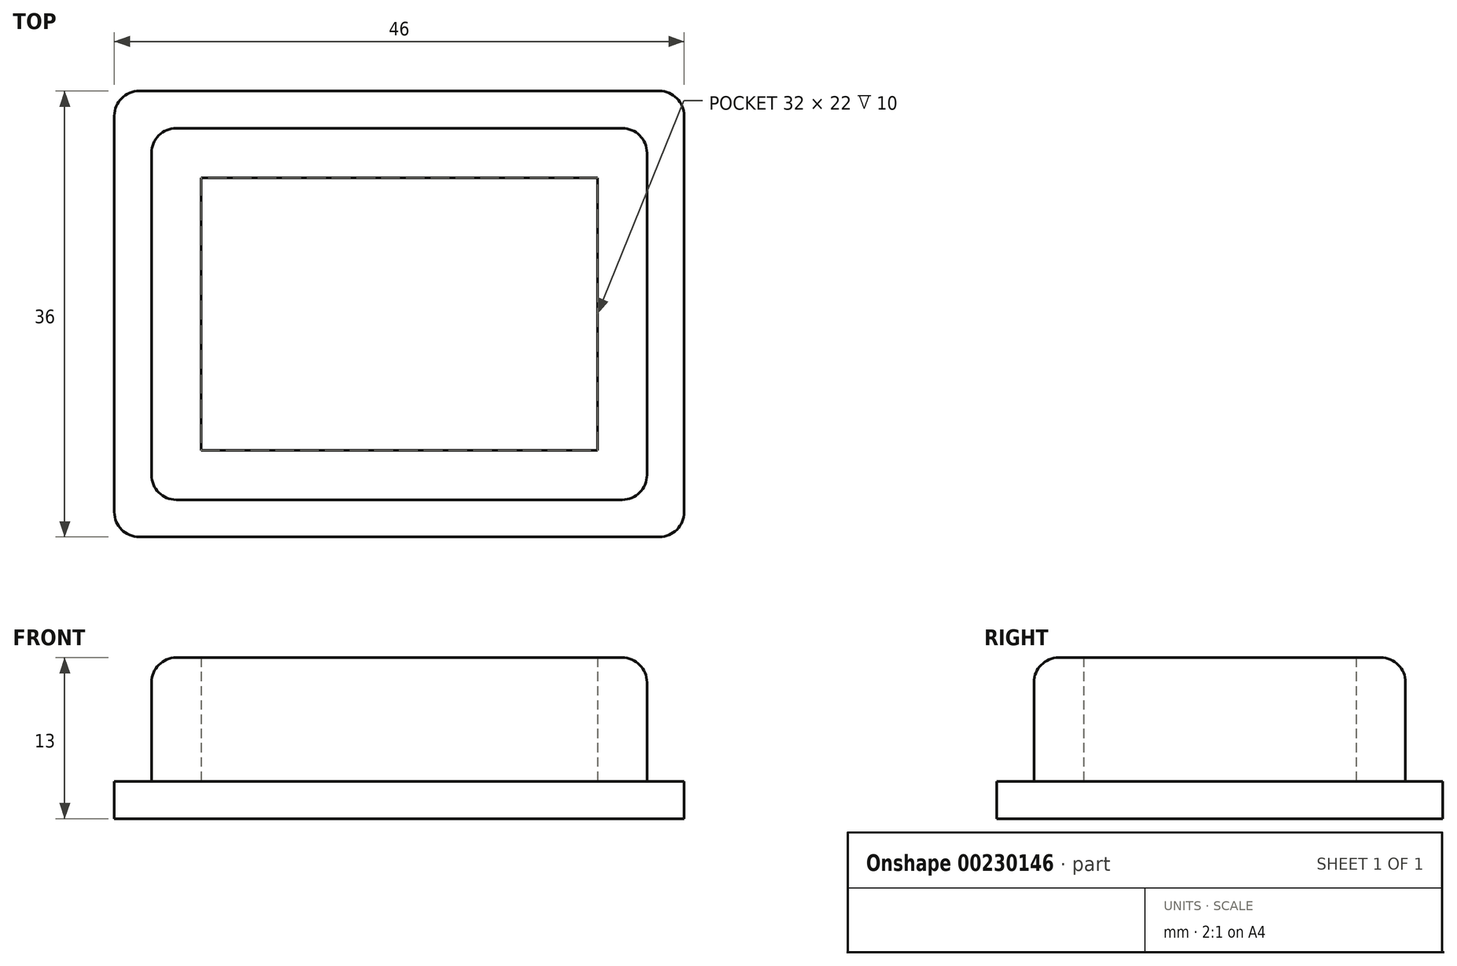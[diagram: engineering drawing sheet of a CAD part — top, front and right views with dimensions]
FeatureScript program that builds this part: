
annotation { "Feature Type Name" : "Feature", "Feature Type Description" : "" }
export const myFeature = defineFeature(function(context is Context, id is Id, definition is map)
    precondition{}
    {
        {
            var Q0;
            Q0=qCreatedBy(makeId("Top.planeOp"),FACE);
            var sketch = newSketch(context, id + "F0", { "sketchPlane" : qUnion([Q0])});
            skLineSegment(sketch, "E0.bottom", {"start": v(20, -15) * mm, "end": v(-20, -15) * mm});
            skLineSegment(sketch, "E0.top", {"start": v(20, 15) * mm, "end": v(-20, 15) * mm});
            skLineSegment(sketch, "E0.left", {"start": v(20, -15) * mm, "end": v(20, 15) * mm});
            skLineSegment(sketch, "E0.right", {"start": v(-20, -15) * mm, "end": v(-20, 15) * mm});
            skPoint(sketch, "E0.middle", {"position": v(0, 0) * mm});
            skLineSegment(sketch, "E1.0", {"start": v(-16, -11) * mm, "end": v(-16, 11) * mm});
            skLineSegment(sketch, "E1.1", {"start": v(16, -11) * mm, "end": v(-16, -11) * mm});
            skLineSegment(sketch, "E1.2", {"start": v(16, -11) * mm, "end": v(16, 11) * mm});
            skLineSegment(sketch, "E1.3", {"start": v(16, 11) * mm, "end": v(-16, 11) * mm});
            skLineSegment(sketch, "E2.0", {"start": v(23, -18) * mm, "end": v(23, 18) * mm});
            skLineSegment(sketch, "E2.1", {"start": v(23, -18) * mm, "end": v(-23, -18) * mm});
            skLineSegment(sketch, "E2.2", {"start": v(-23, -18) * mm, "end": v(-23, 18) * mm});
            skLineSegment(sketch, "E2.3", {"start": v(23, 18) * mm, "end": v(-23, 18) * mm});
            skSolve(sketch);
        }
        {
            var Q0;
            Q0=makeQuery(id+"F0.imprint","IMPRINT",FACE,{"disambiguationData":[TD([[makeQuery(id+"F0.imprint","IMPRINT",EDGE,{"derivedFrom":sQuery(id+"F0.wireOp",EDGE,"E0.bottom")}),-1.0]])]});
            extrude(context, id + "F1", {"entities" : qUnion([Q0]), "depth" : 10 * mm});
        }
        {
            var Q0;
            Q0=makeQuery(id+"F0.imprint","IMPRINT",FACE,{"disambiguationData":[TD([[makeQuery(id+"F0.imprint","IMPRINT",EDGE,{"derivedFrom":sQuery(id+"F0.wireOp",EDGE,"E0.bottom")}),1.0]])]});
            var Q1;
            Q1=makeQuery(id+"F0.imprint","IMPRINT",FACE,{"disambiguationData":[TD([[makeQuery(id+"F0.imprint","IMPRINT",EDGE,{"derivedFrom":sQuery(id+"F0.wireOp",EDGE,"E0.bottom")}),-1.0]])]});
            var Q2;
            Q2=makeQuery(id+"F0.imprint","IMPRINT",FACE,{"disambiguationData":[TD([[makeQuery(id+"F0.imprint","IMPRINT",EDGE,{"derivedFrom":sQuery(id+"F0.wireOp",EDGE,"E1.0")}),-1.0]])]});
            extrude(context, id + "F2", {"entities" : qUnion([Q0, Q1, Q2]), "operationType" : NewBodyOperationType.ADD, "oppositeDirection" : true, "depth" : 3 * mm});
        }
        {
            var Q0;
            Q0=makeQuery(id+"F1.opExtrude","SWEPT_EDGE",EDGE,{"disambiguationData":[OSD([sQuery(id+"F0.wireOp",EDGE,"E0.bottom"),sQuery(id+"F0.wireOp",EDGE,"E0.right")])]});
            var Q1;
            Q1=makeQuery(id+"F1.opExtrude","SWEPT_EDGE",EDGE,{"disambiguationData":[OSD([sQuery(id+"F0.wireOp",EDGE,"E0.top"),sQuery(id+"F0.wireOp",EDGE,"E0.right")])]});
            var Q2;
            Q2=makeQuery(id+"F1.opExtrude","SWEPT_EDGE",EDGE,{"disambiguationData":[OSD([sQuery(id+"F0.wireOp",EDGE,"E0.bottom"),sQuery(id+"F0.wireOp",EDGE,"E0.left")])]});
            var Q3;
            Q3=makeQuery(id+"F1.opExtrude","CAP_EDGE",EDGE,{"disambiguationData":[OSD([sQuery(id+"F0.wireOp",EDGE,"E0.bottom")])],"isStart":false});
            var Q4;
            Q4=makeQuery(id+"F1.opExtrude","CAP_EDGE",EDGE,{"disambiguationData":[OSD([sQuery(id+"F0.wireOp",EDGE,"E0.right")])],"isStart":false});
            var Q5;
            Q5=makeQuery(id+"F1.opExtrude","CAP_EDGE",EDGE,{"disambiguationData":[OSD([sQuery(id+"F0.wireOp",EDGE,"E0.top")])],"isStart":false});
            var Q6;
            Q6=makeQuery(id+"F1.opExtrude","CAP_EDGE",EDGE,{"disambiguationData":[OSD([sQuery(id+"F0.wireOp",EDGE,"E0.left")])],"isStart":false});
            var Q7;
            Q7=makeQuery(id+"F1.opExtrude","SWEPT_EDGE",EDGE,{"disambiguationData":[OSD([sQuery(id+"F0.wireOp",EDGE,"E0.top"),sQuery(id+"F0.wireOp",EDGE,"E0.left")])]});
            var Q8;
            Q8=makeQuery(id+"F2.opExtrude","SWEPT_EDGE",EDGE,{"disambiguationData":[OSD([sQuery(id+"F0.wireOp",EDGE,"E2.0"),sQuery(id+"F0.wireOp",EDGE,"E2.3")])]});
            var Q9;
            Q9=makeQuery(id+"F2.opExtrude","SWEPT_EDGE",EDGE,{"disambiguationData":[OSD([sQuery(id+"F0.wireOp",EDGE,"E2.0"),sQuery(id+"F0.wireOp",EDGE,"E2.1")])]});
            var Q10;
            Q10=makeQuery(id+"F2.opExtrude","SWEPT_EDGE",EDGE,{"disambiguationData":[OSD([sQuery(id+"F0.wireOp",EDGE,"E2.1"),sQuery(id+"F0.wireOp",EDGE,"E2.2")])]});
            var Q11;
            Q11=makeQuery(id+"F2.opExtrude","SWEPT_EDGE",EDGE,{"disambiguationData":[OSD([sQuery(id+"F0.wireOp",EDGE,"E2.2"),sQuery(id+"F0.wireOp",EDGE,"E2.3")])]});
            fillet(context, id + "F3", {"entities" : qUnion([Q0, Q1, Q2, Q3, Q4, Q5, Q6, Q7, Q8, Q9, Q10, Q11]), "radius" : 2 * mm, "tangentPropagation" : true, "allowEdgeOverflow" : false});
        }
    });
